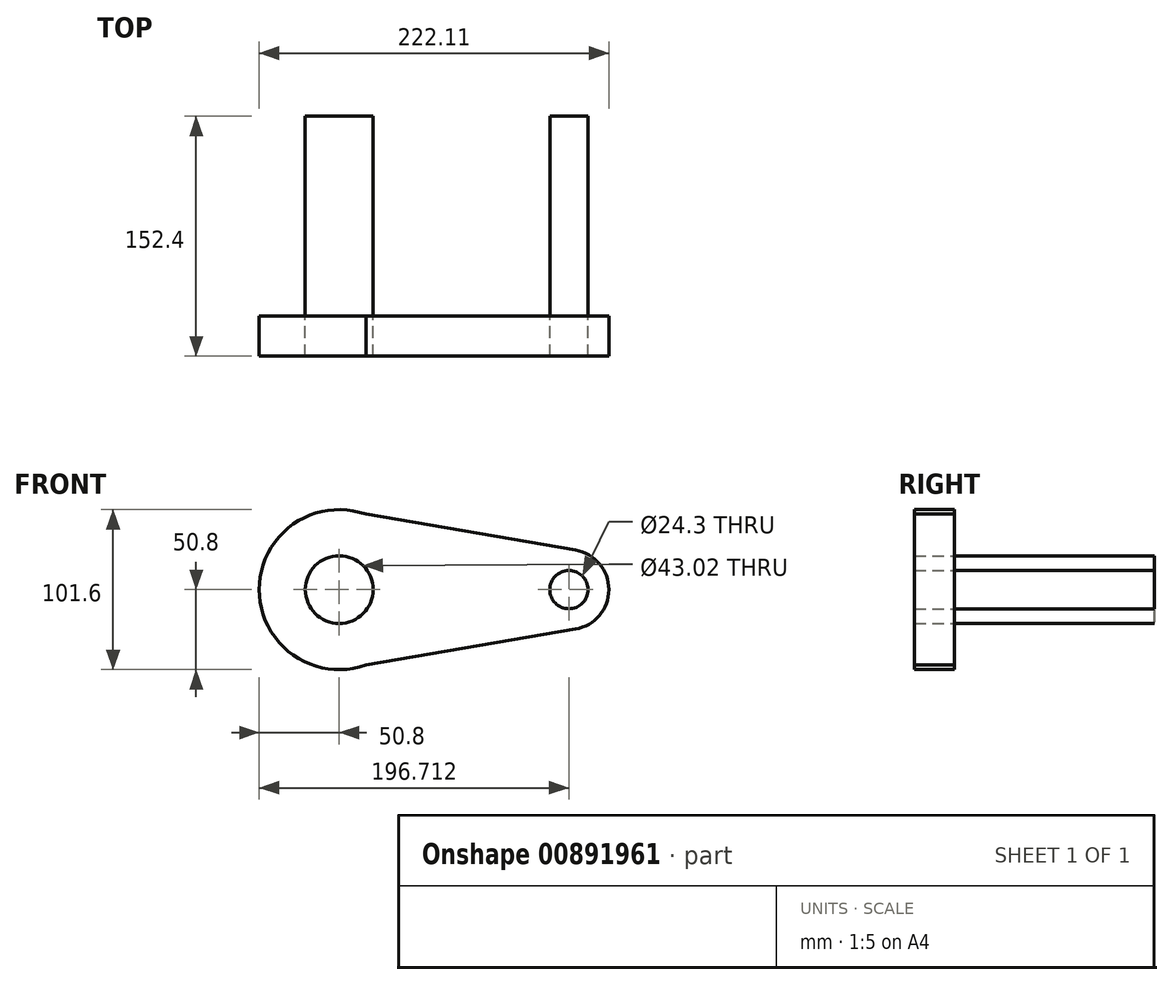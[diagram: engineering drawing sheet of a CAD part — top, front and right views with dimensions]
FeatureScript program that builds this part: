
annotation { "Feature Type Name" : "Feature", "Feature Type Description" : "" }
export const myFeature = defineFeature(function(context is Context, id is Id, definition is map)
    precondition{}
    {
        {
            var Q0;
            Q0=qCreatedBy(makeId("Front.planeOp"),FACE);
            var sketch = newSketch(context, id + "F0", { "sketchPlane" : qUnion([Q0])});
            skCircle(sketch, "E0", {"center": v(0, 0) * mm, "radius": 50.8 * mm});
            skCircle(sketch, "E1", {"center": v(145.91, 0) * mm, "radius": 25.4 * mm});
            skLineSegment(sketch, "E2", {"start": v(0, 50.8) * mm, "end": v(150.2, 25.03) * mm});
            skLineSegment(sketch, "E3", {"start": v(0, -50.8) * mm, "end": v(150.2, -25.03) * mm});
            skCircle(sketch, "E4", {"center": v(0, 0) * mm, "radius": 21.51 * mm});
            skCircle(sketch, "E5", {"center": v(145.91, 0) * mm, "radius": 12.15 * mm});
            skSolve(sketch);
        }
        {
            var Q0;
            Q0 = qSketchRegion(id + "F0", true);
            extrude(context, id + "F1", {"entities" : qUnion([Q0]), "depth" : 25.4 * mm, "offsetDistance" : 25.4 * mm});
        }
        {
            var Q0;
            Q0=makeQuery(id+"F0.imprint","IMPRINT",FACE,{"disambiguationData":[TD([[makeQuery(id+"F0.imprint","IMPRINT",EDGE,{"derivedFrom":sQuery(id+"F0.wireOp",EDGE,"E4")}),1.0]])]});
            var Q1;
            Q1=makeQuery(id+"F0.imprint","IMPRINT",FACE,{"disambiguationData":[TD([[makeQuery(id+"F0.imprint","IMPRINT",EDGE,{"derivedFrom":sQuery(id+"F0.wireOp",EDGE,"E5")}),1.0]])]});
            extrude(context, id + "F2", {"entities" : qUnion([Q0, Q1]), "oppositeDirection" : true, "depth" : 127 * mm, "offsetDistance" : 25.4 * mm});
        }
    });
